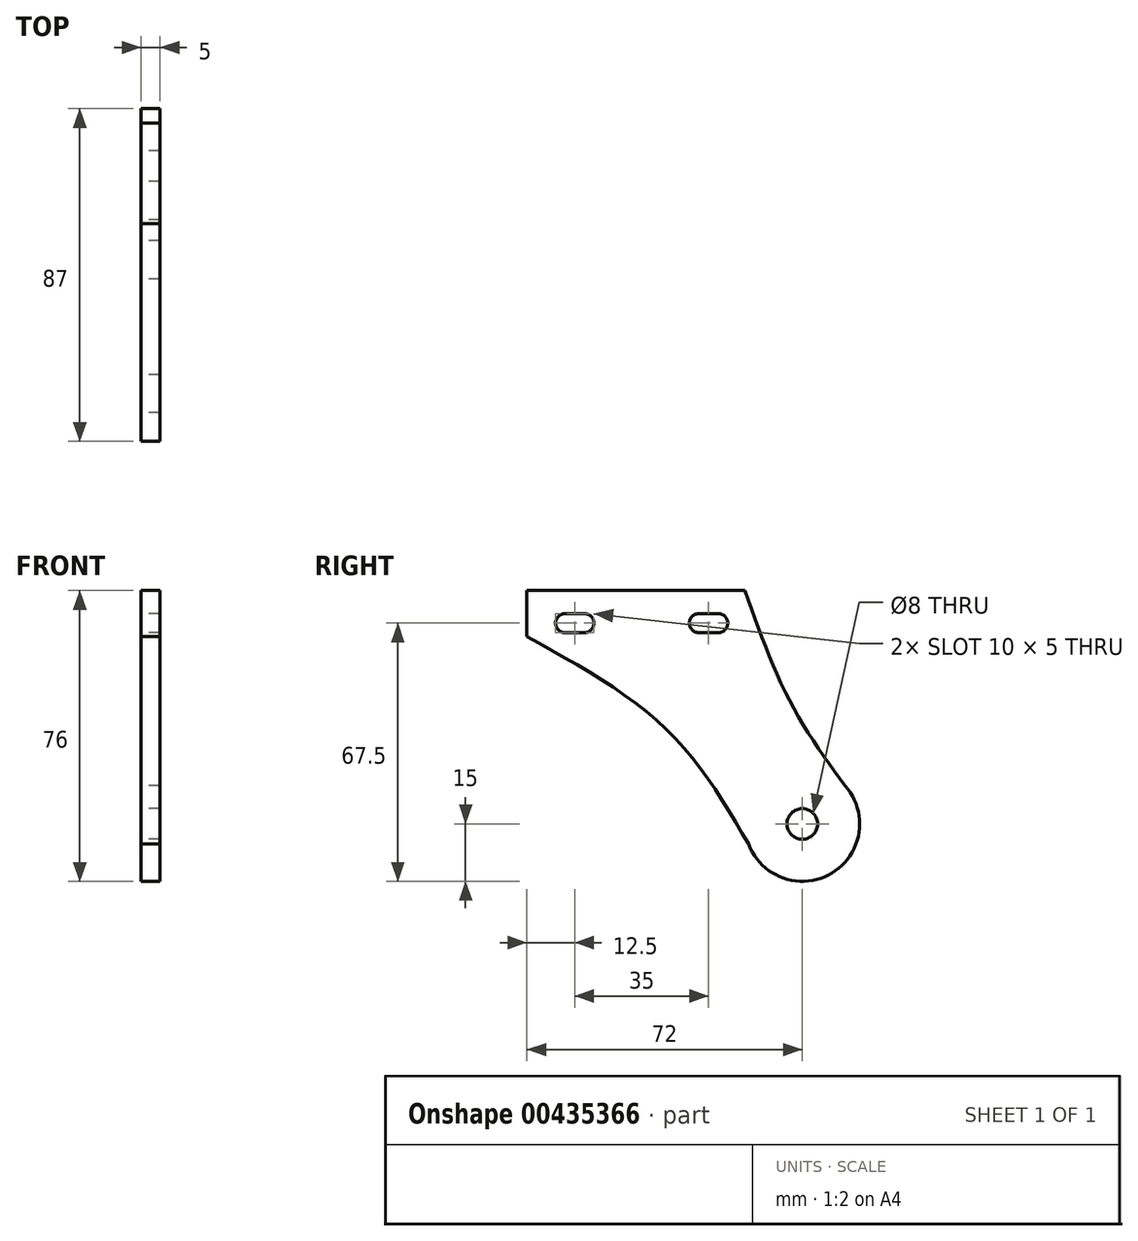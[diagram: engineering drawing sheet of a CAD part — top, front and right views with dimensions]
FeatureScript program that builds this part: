
annotation { "Feature Type Name" : "Feature", "Feature Type Description" : "" }
export const myFeature = defineFeature(function(context is Context, id is Id, definition is map)
    precondition{}
    {
        {
            var Q0;
            Q0=qCreatedBy(makeId("Right.planeOp"),FACE);
            var sketch = newSketch(context, id + "F0", { "sketchPlane" : qUnion([Q0])});
            skCircle(sketch, "E0", {"center": v(0, 0) * mm, "radius": 4 * mm});
            skLineSegment(sketch, "E1", {"start": v(-27, 50) * mm, "end": v(-27, 49.5) * mm});
            skLineSegment(sketch, "E2", {"start": v(-22, 49.5) * mm, "end": v(-22, 50) * mm});
            skArc(sketch, "E3", {"start": v(-14.04, -5.29) * mm, "mid": v(7.76, -12.83) * mm, "end": v(11.2, 9.98) * mm});
            skLineSegment(sketch, "E4", {"start": v(-15, 61) * mm, "end": v(-72, 61) * mm});
            skLineSegment(sketch, "E5", {"start": v(-72, 61) * mm, "end": v(-72, 49) * mm});
            skPoint(sketch, "E6.start.orphan", {"position": v(7.27, 32.34) * mm});
            skFitSpline(sketch, "E7", {"points": [v(-72, 49) * mm, v(-35.65, 24.86) * mm, v(-14.04, -5.29) * mm], "startDerivative": vector(76.31, -42.12) * mm, "endDerivative": vector(39.12, -66.77) * mm});
            skPoint(sketch, "E8.end.orphan", {"position": v(-10.45, -10.76) * mm});
            skPoint(sketch, "E8.start.orphan", {"position": v(-41.22, 19.12) * mm});
            skFitSpline(sketch, "E9", {"points": [v(-15, 61) * mm, v(-2.89, 31.4) * mm, v(12.8, 7.82) * mm], "startDerivative": vector(21.23, -59.74) * mm, "endDerivative": vector(34.51, -46.49) * mm});
            skPoint(sketch, "E10.start.orphan", {"position": v(-0.23, 32.78) * mm});
            skPoint(sketch, "E11.0.internal.orphan", {"position": v(0, 61) * mm});
            skPoint(sketch, "E11.2.internal.orphan", {"position": v(14.54, 3.69) * mm});
            skPoint(sketch, "E12.end.orphan", {"position": v(14.54, 4.57) * mm});
            skPoint(sketch, "E13.start.orphan", {"position": v(-22, 55.5) * mm});
            skArc(sketch, "E14", {"start": v(-62, 55) * mm, "mid": v(-64.5, 52.5) * mm, "end": v(-62, 50) * mm});
            skArc(sketch, "E15", {"start": v(-57, 50) * mm, "mid": v(-54.5, 52.5) * mm, "end": v(-57, 55) * mm});
            skArc(sketch, "E16", {"start": v(-27, 55) * mm, "mid": v(-29.5, 52.5) * mm, "end": v(-27, 50) * mm});
            skArc(sketch, "E17", {"start": v(-22, 50) * mm, "mid": v(-19.5, 52.5) * mm, "end": v(-22, 55) * mm});
            skLineSegment(sketch, "E18", {"start": v(-57, 55) * mm, "end": v(-62, 55) * mm});
            skLineSegment(sketch, "E19", {"start": v(-62, 50) * mm, "end": v(-57, 50) * mm});
            skPoint(sketch, "E20.orphan", {"position": v(-62, 55.5) * mm});
            skPoint(sketch, "E21.orphan", {"position": v(-57, 55.5) * mm});
            skLineSegment(sketch, "E22", {"start": v(-27, 50) * mm, "end": v(-22, 50) * mm});
            skLineSegment(sketch, "E23", {"start": v(-22, 55) * mm, "end": v(-27, 55) * mm});
            skSolve(sketch);
        }
        {
            var Q0;
            Q0 = qSketchRegion(id + "F0", true);
            extrude(context, id + "F1", {"entities" : qUnion([Q0]), "depth" : 5 * mm, "offsetDistance" : 25 * mm});
        }
    });
